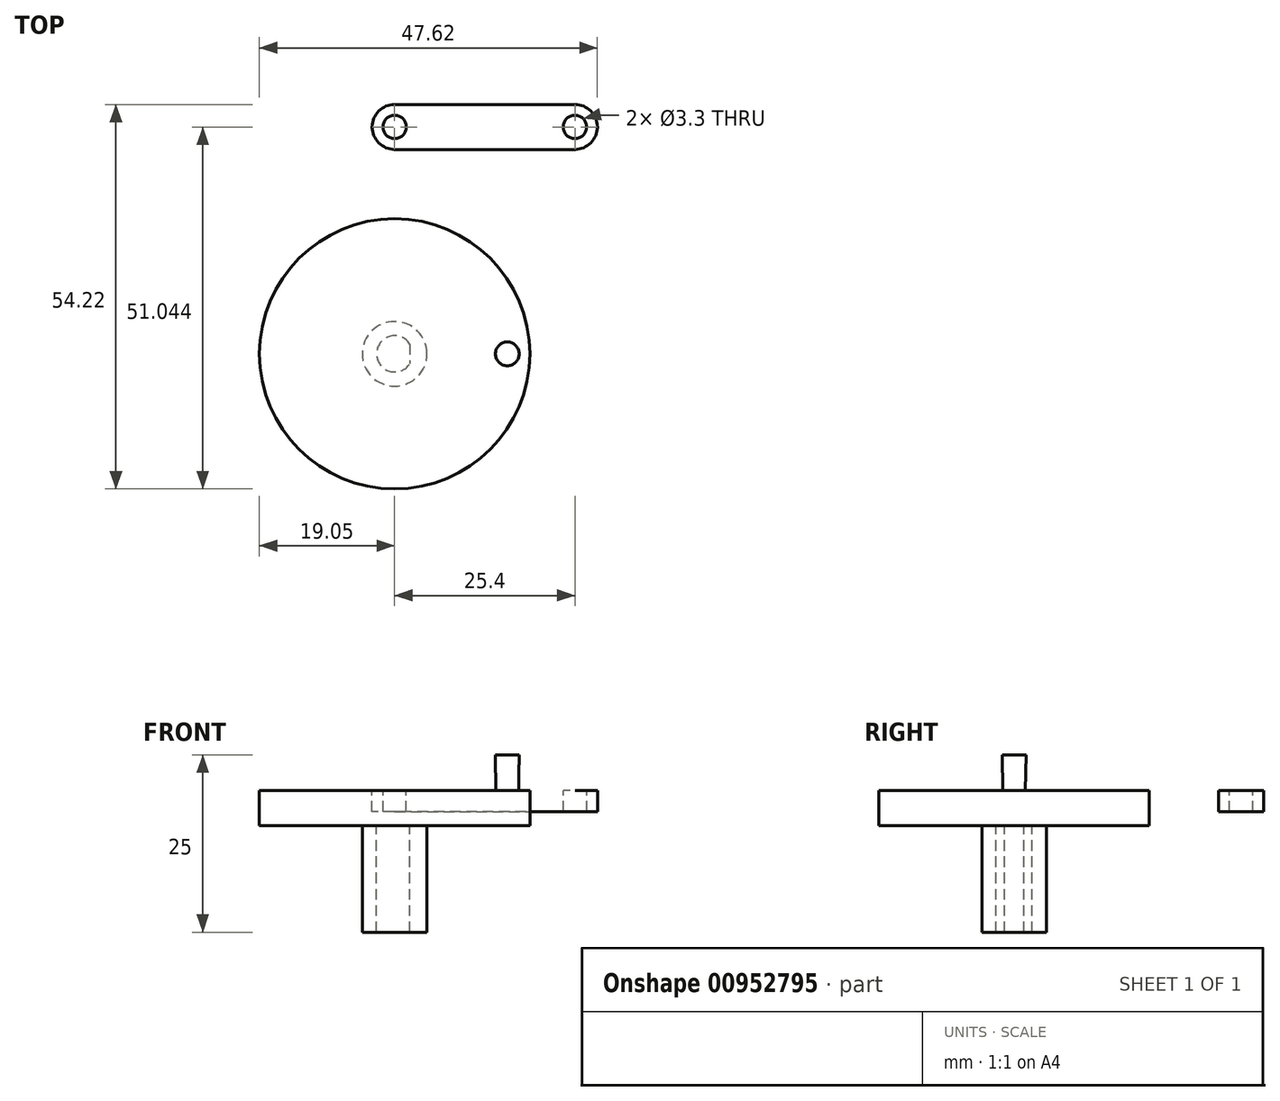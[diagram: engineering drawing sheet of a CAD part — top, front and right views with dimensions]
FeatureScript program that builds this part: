
annotation { "Feature Type Name" : "Feature", "Feature Type Description" : "" }
export const myFeature = defineFeature(function(context is Context, id is Id, definition is map)
    precondition{}
    {
        {
            var Q0;
            Q0=qCreatedBy(makeId("Top.planeOp"),FACE);
            var sketch = newSketch(context, id + "F0", { "sketchPlane" : qUnion([Q0])});
            skCircle(sketch, "E0", {"center": v(0, 0) * mm, "radius": 19.05 * mm});
            skArc(sketch, "E1", {"start": v(2.15, 1.37) * mm, "mid": v(-2.55, 0) * mm, "end": v(2.15, -1.37) * mm});
            skLineSegment(sketch, "E2", {"start": v(2.15, 1.37) * mm, "end": v(2.15, -1.37) * mm});
            skPoint(sketch, "E3.orphan", {"position": v(2.15, 3.33) * mm});
            skPoint(sketch, "E4.orphan", {"position": v(2.15, 0) * mm});
            skPoint(sketch, "E5.start.orphan", {"position": v(-2.55, 0) * mm});
            skCircle(sketch, "E6", {"center": v(0, 0) * mm, "radius": 4.55 * mm});
            skLineSegment(sketch, "E7", {"start": v(0, 32) * mm, "end": v(25.4, 32) * mm});
            skCircle(sketch, "E8", {"center": v(0, 32) * mm, "radius": 3.18 * mm});
            skCircle(sketch, "E9", {"center": v(25.4, 32) * mm, "radius": 3.18 * mm});
            skLineSegment(sketch, "E10", {"start": v(25.4, 35.17) * mm, "end": v(0, 35.17) * mm});
            skCircle(sketch, "E11", {"center": v(0, 32) * mm, "radius": 1.65 * mm});
            skLineSegment(sketch, "E12", {"start": v(0, 28.82) * mm, "end": v(25.4, 28.82) * mm});
            skCircle(sketch, "E13", {"center": v(25.4, 32) * mm, "radius": 1.65 * mm});
            skSolve(sketch);
        }
        {
            var Q0;
            Q0=makeQuery(id+"F0.imprint","IMPRINT",FACE,{"disambiguationData":[TD([[makeQuery(id+"F0.imprint","IMPRINT",EDGE,{"derivedFrom":sQuery(id+"F0.wireOp",EDGE,"E1")}),1.0]])]});
            var Q1;
            Q1=makeQuery(id+"F0.imprint","IMPRINT",FACE,{"disambiguationData":[TD([[makeQuery(id+"F0.imprint","IMPRINT",EDGE,{"derivedFrom":sQuery(id+"F0.wireOp",EDGE,"E0")}),1.0]])]});
            extrude(context, id + "F1", {"entities" : qUnion([Q0, Q1]), "oppositeDirection" : true, "depth" : 5 * mm});
        }
        {
            var Q0;
            Q0=makeQuery(id+"F0.imprint","IMPRINT",FACE,{"disambiguationData":[TD([[makeQuery(id+"F0.imprint","IMPRINT",EDGE,{"derivedFrom":sQuery(id+"F0.wireOp",EDGE,"E1")}),-1.0]])]});
            extrude(context, id + "F2", {"entities" : qUnion([Q0]), "operationType" : NewBodyOperationType.ADD, "oppositeDirection" : true, "depth" : 20 * mm});
        }
        {
            var Q0;
            {var subQ0=sQuery(id+"F0.wireOp",EDGE,"E6");var subQ1=sQuery(id+"F0.wireOp",EDGE,"E2");var subQ2=sQuery(id+"F0.wireOp",EDGE,"E1");Q0=makeQuery(id+"F2.boolean.opBoolean","MERGE",FACE,{"derivedFrom":[makeQuery(id+"F1.opExtrude","CAP_FACE",FACE,{"disambiguationData":[OSD([sQuery(id+"F0.wireOp",EDGE,"E0"),subQ0])],"isStart":true}),makeQuery(id+"F1.opExtrude","CAP_FACE",FACE,{"disambiguationData":[OSD([subQ2,subQ1])],"isStart":true}),makeQuery(id+"F2.opExtrude","CAP_FACE",FACE,{"disambiguationData":[OSD([subQ2,subQ1,subQ0])],"isStart":true})]});}
            var sketch = newSketch(context, id + "F3", { "sketchPlane" : qUnion([Q0])});
            skCircle(sketch, "E14", {"center": v(0, 0) * mm, "radius": 15.88 * mm});
            skCircle(sketch, "E15", {"center": v(15.88, 0) * mm, "radius": 1.59 * mm});
            skSolve(sketch);
        }
        {
            var Q0;
            {var subQ0=sQuery(id+"F3.wireOp",EDGE,"E15");var subQ1=sQuery(id+"F3.wireOp",EDGE,"E14");var subQ2=makeQuery(id+"F3.imprint","INTERSECT",VERTEX,{"disambiguationData":[OD(0.0)],"derivedFrom":[subQ1,subQ0]});Q0=makeQuery(id+"F3.imprint","IMPRINT",FACE,{"disambiguationData":[TD([[makeQuery(id+"F3.imprint","IMPRINT",EDGE,{"disambiguationData":[TD([[subQ2,-1.0]])],"derivedFrom":subQ1}),1.0]])]});}
            var Q1;
            {var subQ0=sQuery(id+"F3.wireOp",EDGE,"E15");var subQ1=sQuery(id+"F3.wireOp",EDGE,"E14");var subQ2=makeQuery(id+"F3.imprint","INTERSECT",VERTEX,{"disambiguationData":[OD(0.0)],"derivedFrom":[subQ1,subQ0]});Q1=makeQuery(id+"F3.imprint","IMPRINT",FACE,{"disambiguationData":[TD([[makeQuery(id+"F3.imprint","IMPRINT",EDGE,{"disambiguationData":[TD([[subQ2,-1.0]])],"derivedFrom":subQ1}),-1.0]])]});}
            extrude(context, id + "F4", {"entities" : qUnion([Q0, Q1]), "operationType" : NewBodyOperationType.ADD, "depth" : 5 * mm, "hasDraft" : true, "draftAngle" : 1 * degree});
        }
        {
            var Q0;
            Q0=makeQuery(id+"F0.imprint","IMPRINT",FACE,{"disambiguationData":[TD([[makeQuery(id+"F0.imprint","IMPRINT",EDGE,{"derivedFrom":sQuery(id+"F0.wireOp",EDGE,"E11")}),-1.0]])]});
            var Q1;
            {var subQ5=sQuery(id+"F0.wireOp",EDGE,"E12");Q1=makeQuery(id+"F0.imprint","IMPRINT",FACE,{"disambiguationData":[TD([[makeQuery(id+"F0.imprint","IMPRINT",EDGE,{"derivedFrom":subQ5}),1.0]])]});}
            var Q2;
            {var subQ5=sQuery(id+"F0.wireOp",EDGE,"E10");Q2=makeQuery(id+"F0.imprint","IMPRINT",FACE,{"disambiguationData":[TD([[makeQuery(id+"F0.imprint","IMPRINT",EDGE,{"derivedFrom":subQ5}),1.0]])]});}
            var Q3;
            Q3=makeQuery(id+"F0.imprint","IMPRINT",FACE,{"disambiguationData":[TD([[makeQuery(id+"F0.imprint","IMPRINT",EDGE,{"derivedFrom":sQuery(id+"F0.wireOp",EDGE,"E13")}),-1.0]])]});
            extrude(context, id + "F5", {"entities" : qUnion([Q0, Q1, Q2, Q3]), "oppositeDirection" : true, "depth" : 3 * mm});
        }
    });
